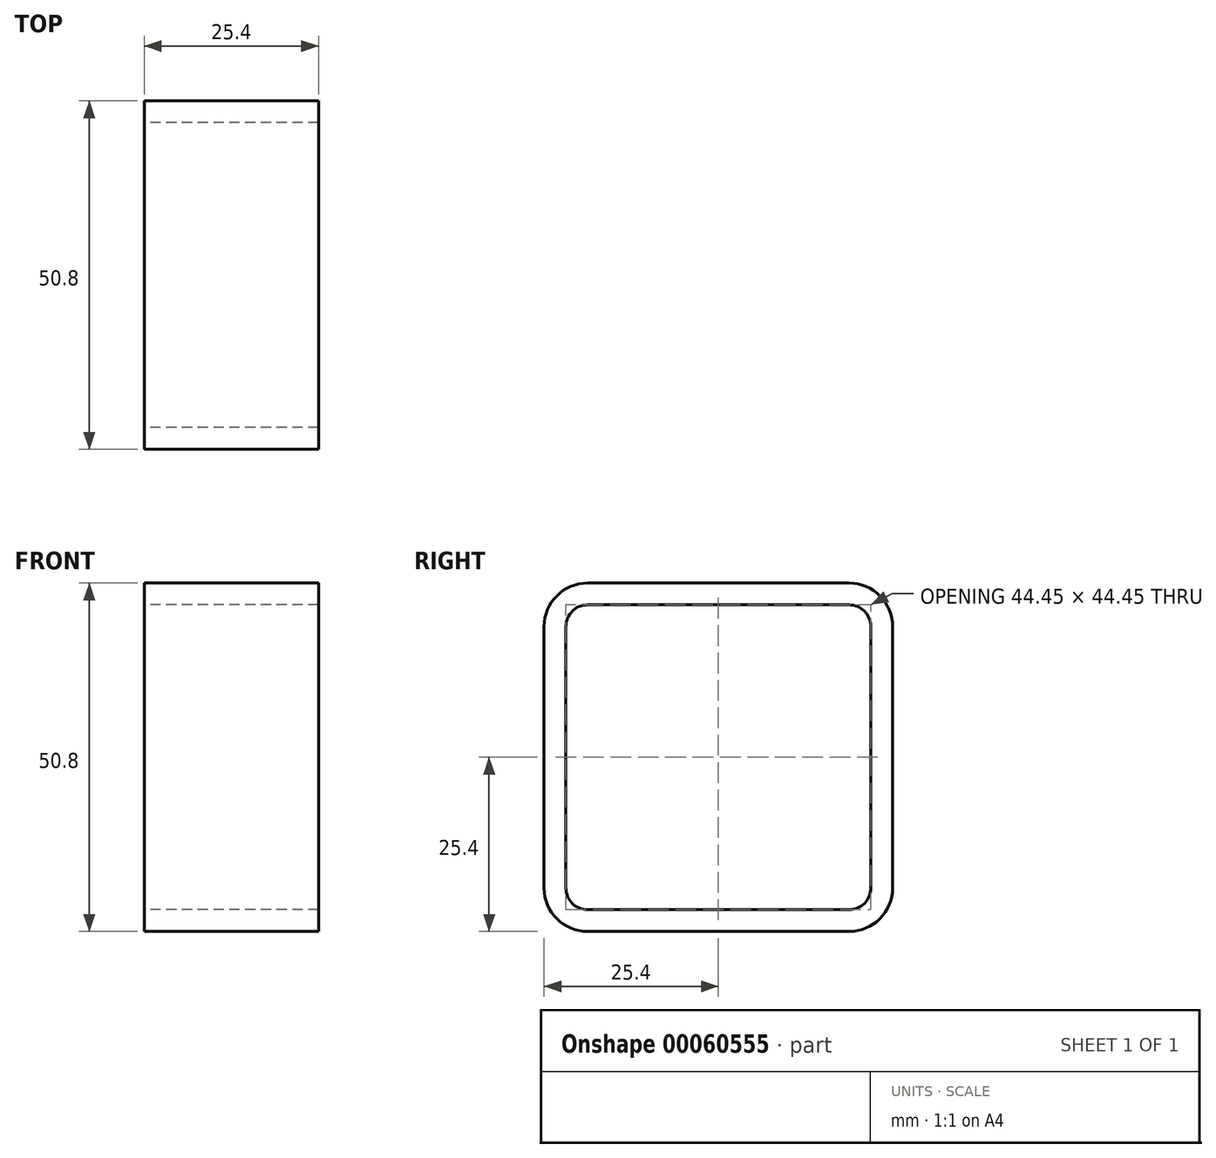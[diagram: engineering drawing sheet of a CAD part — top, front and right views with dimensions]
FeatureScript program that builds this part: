
annotation { "Feature Type Name" : "Feature", "Feature Type Description" : "" }
export const myFeature = defineFeature(function(context is Context, id is Id, definition is map)
    precondition{}
    {
        {
            var Q0;
            Q0=qCreatedBy(makeId("Right.planeOp"),FACE);
            var sketch = newSketch(context, id + "F0", { "sketchPlane" : qUnion([Q0])});
            skLineSegment(sketch, "E0.bottom", {"start": v(-19.05, 25.4) * mm, "end": v(19.05, 25.4) * mm});
            skLineSegment(sketch, "E0.top", {"start": v(-19.05, -25.4) * mm, "end": v(19.05, -25.4) * mm});
            skLineSegment(sketch, "E0.left", {"start": v(-25.4, 19.05) * mm, "end": v(-25.4, -19.05) * mm});
            skLineSegment(sketch, "E0.right", {"start": v(25.4, 19.05) * mm, "end": v(25.4, -19.05) * mm});
            skLineSegment(sketch, "E1.bottom", {"start": v(-19.05, 22.23) * mm, "end": v(19.05, 22.23) * mm});
            skLineSegment(sketch, "E1.top", {"start": v(-19.05, -22.23) * mm, "end": v(19.05, -22.23) * mm});
            skLineSegment(sketch, "E1.left", {"start": v(-22.23, 19.05) * mm, "end": v(-22.23, -19.05) * mm});
            skLineSegment(sketch, "E1.right", {"start": v(22.23, 19.05) * mm, "end": v(22.23, -19.05) * mm});
            skPoint(sketch, "E2.visualSharp", {"position": v(-25.4, 25.4) * mm});
            skArc(sketch, "E2.filletArc", {"start": v(-19.05, 25.4) * mm, "mid": v(-23.54, 23.54) * mm, "end": v(-25.4, 19.05) * mm});
            skPoint(sketch, "E3.visualSharp", {"position": v(-22.23, 22.23) * mm});
            skArc(sketch, "E3.filletArc", {"start": v(-19.05, 22.23) * mm, "mid": v(-21.3, 21.3) * mm, "end": v(-22.23, 19.05) * mm});
            skPoint(sketch, "E4.visualSharp", {"position": v(-25.4, -25.4) * mm});
            skArc(sketch, "E4.filletArc", {"start": v(-25.4, -19.05) * mm, "mid": v(-23.54, -23.54) * mm, "end": v(-19.05, -25.4) * mm});
            skPoint(sketch, "E5.visualSharp", {"position": v(25.4, -25.4) * mm});
            skArc(sketch, "E5.filletArc", {"start": v(19.05, -25.4) * mm, "mid": v(23.54, -23.54) * mm, "end": v(25.4, -19.05) * mm});
            skPoint(sketch, "E6.visualSharp", {"position": v(25.4, 25.4) * mm});
            skArc(sketch, "E6.filletArc", {"start": v(25.4, 19.05) * mm, "mid": v(23.54, 23.54) * mm, "end": v(19.05, 25.4) * mm});
            skPoint(sketch, "E7.visualSharp", {"position": v(22.23, 22.23) * mm});
            skArc(sketch, "E7.filletArc", {"start": v(22.23, 19.05) * mm, "mid": v(21.3, 21.3) * mm, "end": v(19.05, 22.23) * mm});
            skPoint(sketch, "E8.visualSharp", {"position": v(22.23, -22.23) * mm});
            skArc(sketch, "E8.filletArc", {"start": v(19.05, -22.23) * mm, "mid": v(21.3, -21.3) * mm, "end": v(22.23, -19.05) * mm});
            skPoint(sketch, "E9.visualSharp", {"position": v(-22.23, -22.23) * mm});
            skArc(sketch, "E9.filletArc", {"start": v(-22.23, -19.05) * mm, "mid": v(-21.3, -21.3) * mm, "end": v(-19.05, -22.23) * mm});
            skSolve(sketch);
        }
        {
            var Q0;
            Q0 = qSketchRegion(id + "F0", true);
            extrude(context, id + "F1", {"entities" : qUnion([Q0]), "depth" : 25.4 * mm});
        }
    });
